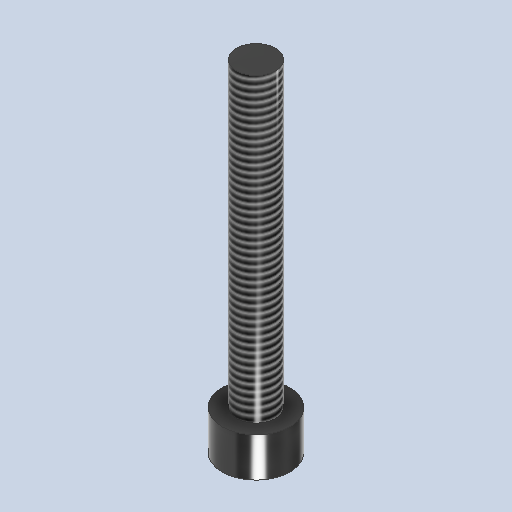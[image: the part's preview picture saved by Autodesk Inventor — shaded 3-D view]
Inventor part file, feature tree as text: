
AUTODESK INVENTOR PART (.ipt)
format: ipt  version: 2024.2 (Build 282272000, 272)  size: 161,280 bytes
history: native  units: mm
features: sketch x2, revolve x1, thread x1, extrude x1
ambient origin geometry x8: Origin, YZ Plane, XZ Plane, XY Plane, X Axis, Y Axis, Z Axis, Center Point
bodies: Solid1 (feature_tree)
feature tree (5):
  revolve  "Revolution1"  [1 undecoded]
  thread  "Thread1"  [1 undecoded]
  extrude  "Extrusion1"  [1 undecoded]
  sketch  "Sketch1"  dims[d4=90.0deg d5=6.0mm d6=0.0mm d0=0.0mm]
  sketch  "Sketch2"
note: 3 required parameter values undecoded (feature->parameter linkage not recoverable at this tier; creation-order binding heuristic only, values carry confidence <= 0.55)